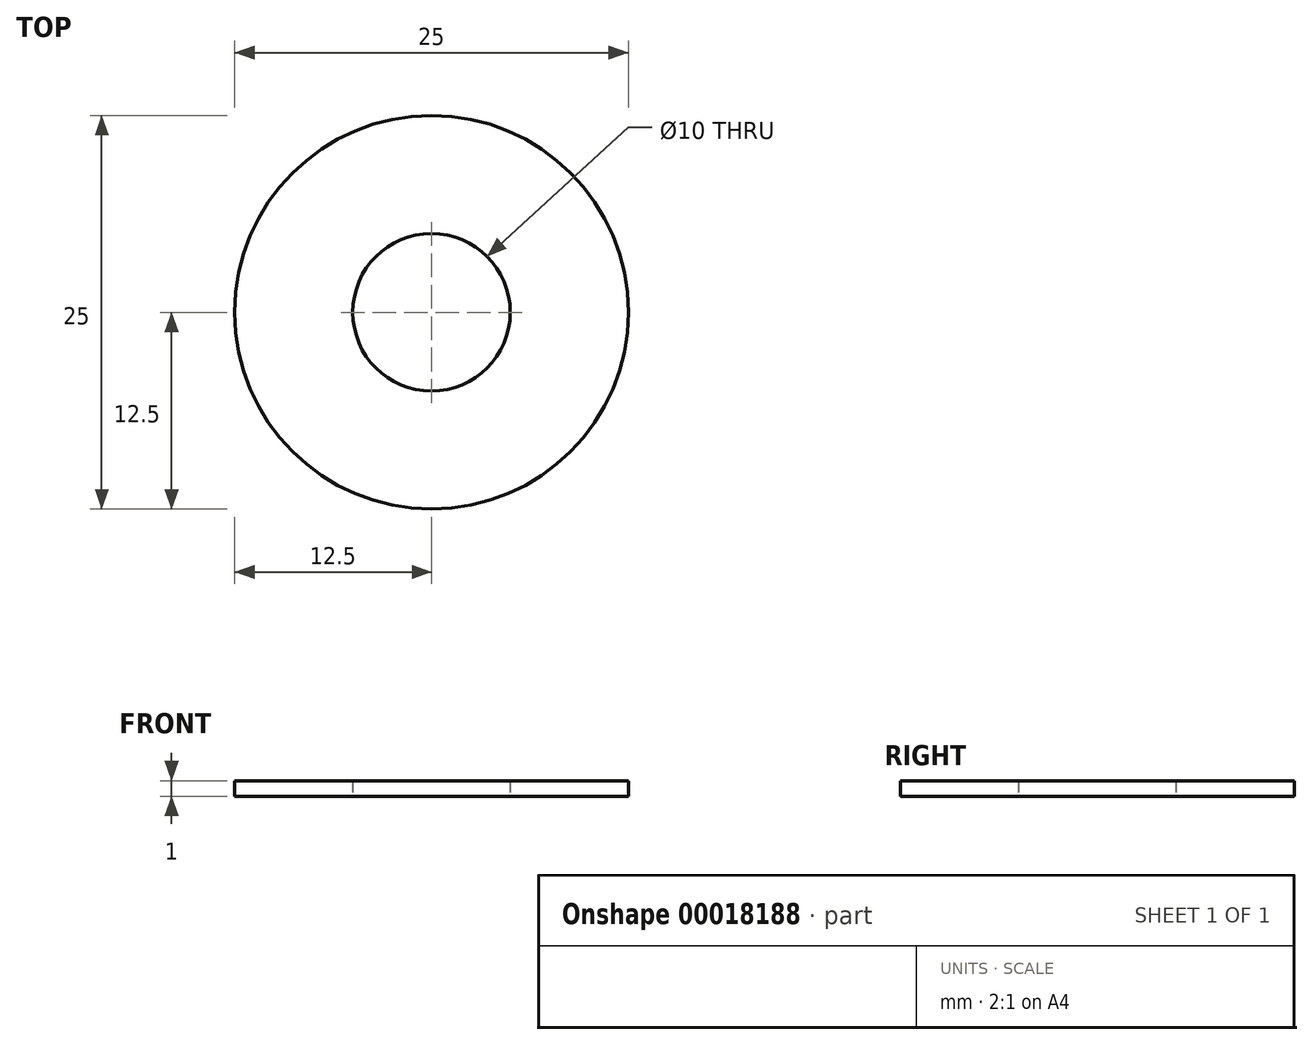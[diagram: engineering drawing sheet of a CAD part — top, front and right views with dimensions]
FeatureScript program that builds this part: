
annotation { "Feature Type Name" : "Feature", "Feature Type Description" : "" }
export const myFeature = defineFeature(function(context is Context, id is Id, definition is map)
    precondition{}
    {
        {
            var Q0;
            Q0=qCreatedBy(makeId("Top.planeOp"),FACE);
            var sketch = newSketch(context, id + "F0", { "sketchPlane" : qUnion([Q0])});
            skCircle(sketch, "E0", {"center": v(0, 0) * mm, "radius": 12.5 * mm});
            skCircle(sketch, "E1", {"center": v(0, 0) * mm, "radius": 5 * mm});
            skSolve(sketch);
        }
        {
            var Q0;
            Q0 = qSketchRegion(id + "F0", true);
            extrude(context, id + "F1", {"entities" : qUnion([Q0]), "depth" : 1 * mm});
        }
    });
